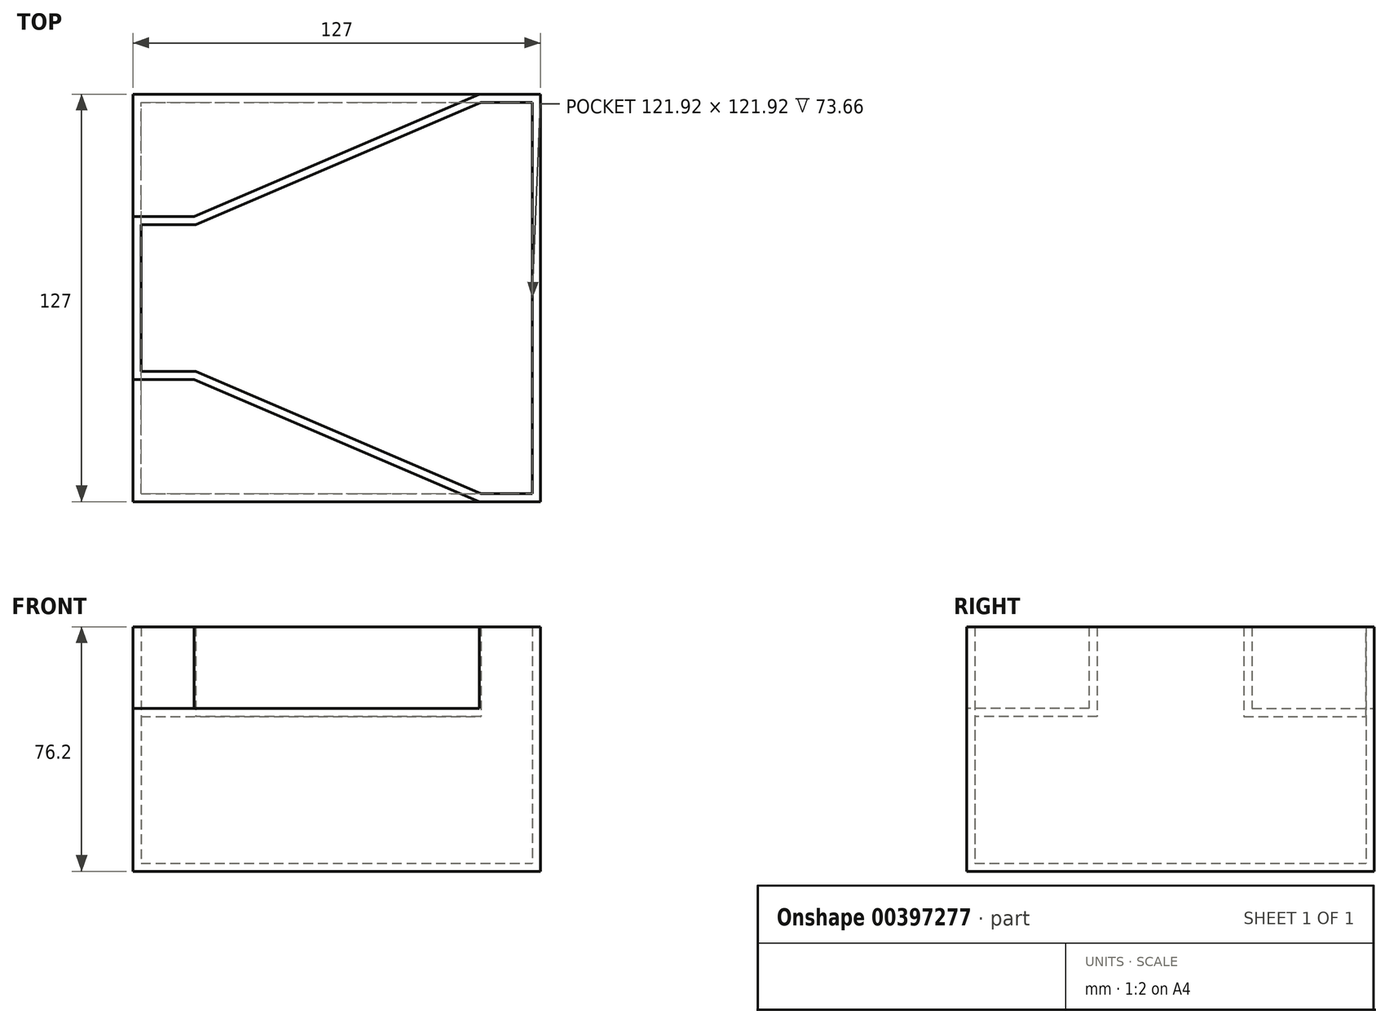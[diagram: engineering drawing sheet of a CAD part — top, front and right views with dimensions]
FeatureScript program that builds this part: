
annotation { "Feature Type Name" : "Feature", "Feature Type Description" : "" }
export const myFeature = defineFeature(function(context is Context, id is Id, definition is map)
    precondition{}
    {
        {
            var Q0;
            Q0=qCreatedBy(makeId("Top.planeOp"),FACE);
            var sketch = newSketch(context, id + "F0", { "sketchPlane" : qUnion([Q0])});
            skLineSegment(sketch, "E0.bottom", {"start": v(0, 0) * mm, "end": v(127, 0) * mm});
            skLineSegment(sketch, "E0.top", {"start": v(0, 127) * mm, "end": v(127, 127) * mm});
            skLineSegment(sketch, "E0.left", {"start": v(0, 0) * mm, "end": v(0, 127) * mm});
            skLineSegment(sketch, "E0.right", {"start": v(127, 0) * mm, "end": v(127, 127) * mm});
            skSolve(sketch);
        }
        {
            var Q0;
            Q0=makeQuery(id+"F0.imprint","IMPRINT",FACE,{"disambiguationData":[TD([[makeQuery(id+"F0.imprint","IMPRINT",EDGE,{"derivedFrom":sQuery(id+"F0.wireOp",EDGE,"E0.bottom")}),1.0]])]});
            extrude(context, id + "F1", {"entities" : qUnion([Q0]), "depth" : 50.8 * mm});
        }
        {
            var Q0;
            Q0=makeQuery(id+"F1.opExtrude","CAP_FACE",FACE,{"disambiguationData":[OSD([sQuery(id+"F0.wireOp",EDGE,"E0.bottom"),sQuery(id+"F0.wireOp",EDGE,"E0.top"),sQuery(id+"F0.wireOp",EDGE,"E0.left"),sQuery(id+"F0.wireOp",EDGE,"E0.right")])],"isStart":false});
            var sketch = newSketch(context, id + "F2", { "sketchPlane" : qUnion([Q0])});
            skLineSegment(sketch, "E1.bottom", {"start": v(0, 38.1) * mm, "end": v(19.05, 38.1) * mm});
            skLineSegment(sketch, "E1.top", {"start": v(0, 88.9) * mm, "end": v(19.05, 88.9) * mm});
            skLineSegment(sketch, "E1.left", {"start": v(0, 38.1) * mm, "end": v(0, 88.9) * mm});
            skLineSegment(sketch, "E1.right", {"start": v(19.05, 38.1) * mm, "end": v(19.05, 88.9) * mm});
            skLineSegment(sketch, "E2.bottom", {"start": v(127, 0) * mm, "end": v(107.95, 0) * mm});
            skLineSegment(sketch, "E2.top", {"start": v(127, 127) * mm, "end": v(107.95, 127) * mm});
            skLineSegment(sketch, "E2.left", {"start": v(127, 0) * mm, "end": v(127, 127) * mm});
            skLineSegment(sketch, "E2.right", {"start": v(107.95, 0) * mm, "end": v(107.95, 127) * mm});
            skSolve(sketch);
        }
        {
            var Q0;
            Q0=makeQuery(id+"F2.imprint","IMPRINT",FACE,{"disambiguationData":[TD([[makeQuery(id+"F2.imprint","IMPRINT",EDGE,{"derivedFrom":sQuery(id+"F2.wireOp",EDGE,"E1.bottom")}),1.0]])]});
            var Q1;
            Q1=makeQuery(id+"F2.imprint","IMPRINT",FACE,{"disambiguationData":[TD([[makeQuery(id+"F2.imprint","IMPRINT",EDGE,{"derivedFrom":sQuery(id+"F2.wireOp",EDGE,"E2.bottom")}),1.0]])]});
            extrude(context, id + "F3", {"entities" : qUnion([Q0, Q1]), "operationType" : NewBodyOperationType.ADD, "depth" : 25.4 * mm});
        }
        {
            var Q1;
            Q1=makeQuery(id+"F3.opExtrude","SWEPT_FACE",FACE,{"disambiguationData":[OSD([sQuery(id+"F2.wireOp",EDGE,"E1.right")])]});
            var Q2;
            Q2=makeQuery(id+"F3.opExtrude","SWEPT_FACE",FACE,{"disambiguationData":[OSD([sQuery(id+"F2.wireOp",EDGE,"E2.right")])]});
            loft(context, id + "F4", {"operationType" : NewBodyOperationType.ADD, "sheetProfilesArray" : [{ "sheetProfileEntities" : qUnion([Q1]) }, { "sheetProfileEntities" : qUnion([Q2]) }]});
        }
        {
            var Q0;
            {var subQ0=sQuery(id+"F2.wireOp",EDGE,"E2.right");var subQ1=sQuery(id+"F2.wireOp",EDGE,"E1.right");var subQ2=sQuery(id+"F2.wireOp",EDGE,"E2.top");var subQ3=sQuery(id+"F0.wireOp",EDGE,"E0.top");var subQ4=sQuery(id+"F2.wireOp",EDGE,"E2.bottom");var subQ5=sQuery(id+"F0.wireOp",EDGE,"E0.bottom");var subQ6=sQuery(id+"F2.wireOp",EDGE,"E1.top");var subQ7=sQuery(id+"F2.wireOp",EDGE,"E1.bottom");Q0=makeQuery(id+"F4.boolean.opBoolean","MERGE",FACE,{"derivedFrom":[makeQuery(id+"F3.opExtrude","CAP_FACE",FACE,{"disambiguationData":[OSD([subQ7,subQ6,sQuery(id+"F2.wireOp",EDGE,"E1.left"),subQ1])],"isStart":false}),makeQuery(id+"F3.opExtrude","CAP_FACE",FACE,{"disambiguationData":[OSD([subQ4,subQ2,sQuery(id+"F2.wireOp",EDGE,"E2.left"),subQ0])],"isStart":false}),makeQuery(id+"F4.opLoft","SWEPT_FACE",FACE,{"disambiguationData":[OSD([subQ5,subQ3,subQ7,subQ6,subQ1,subQ4,subQ2,subQ0]),TDD([makeQuery(id+"F3.opExtrude","CAP_VERTEX",VERTEX,{"disambiguationData":[OSD([subQ7,subQ1])],"isStart":false}),makeQuery(id+"F3.opExtrude","CAP_VERTEX",VERTEX,{"disambiguationData":[OSD([subQ6,subQ1])],"isStart":false}),makeQuery(id+"F3.opExtrude","CAP_VERTEX",VERTEX,{"disambiguationData":[OSD([subQ5,subQ4,subQ0])],"isStart":false}),makeQuery(id+"F3.opExtrude","CAP_VERTEX",VERTEX,{"disambiguationData":[OSD([subQ3,subQ2,subQ0])],"isStart":false}),makeQuery(id+"F3.opExtrude","CAP_EDGE",EDGE,{"disambiguationData":[OSD([subQ1])],"isStart":false}),makeQuery(id+"F3.opExtrude","CAP_EDGE",EDGE,{"disambiguationData":[OSD([subQ0])],"isStart":false})])]})]});}
            shell(context, id + "F5", {"entities" : qUnion([Q0]), "thickness" : 2.54 * mm});
        }
    });
